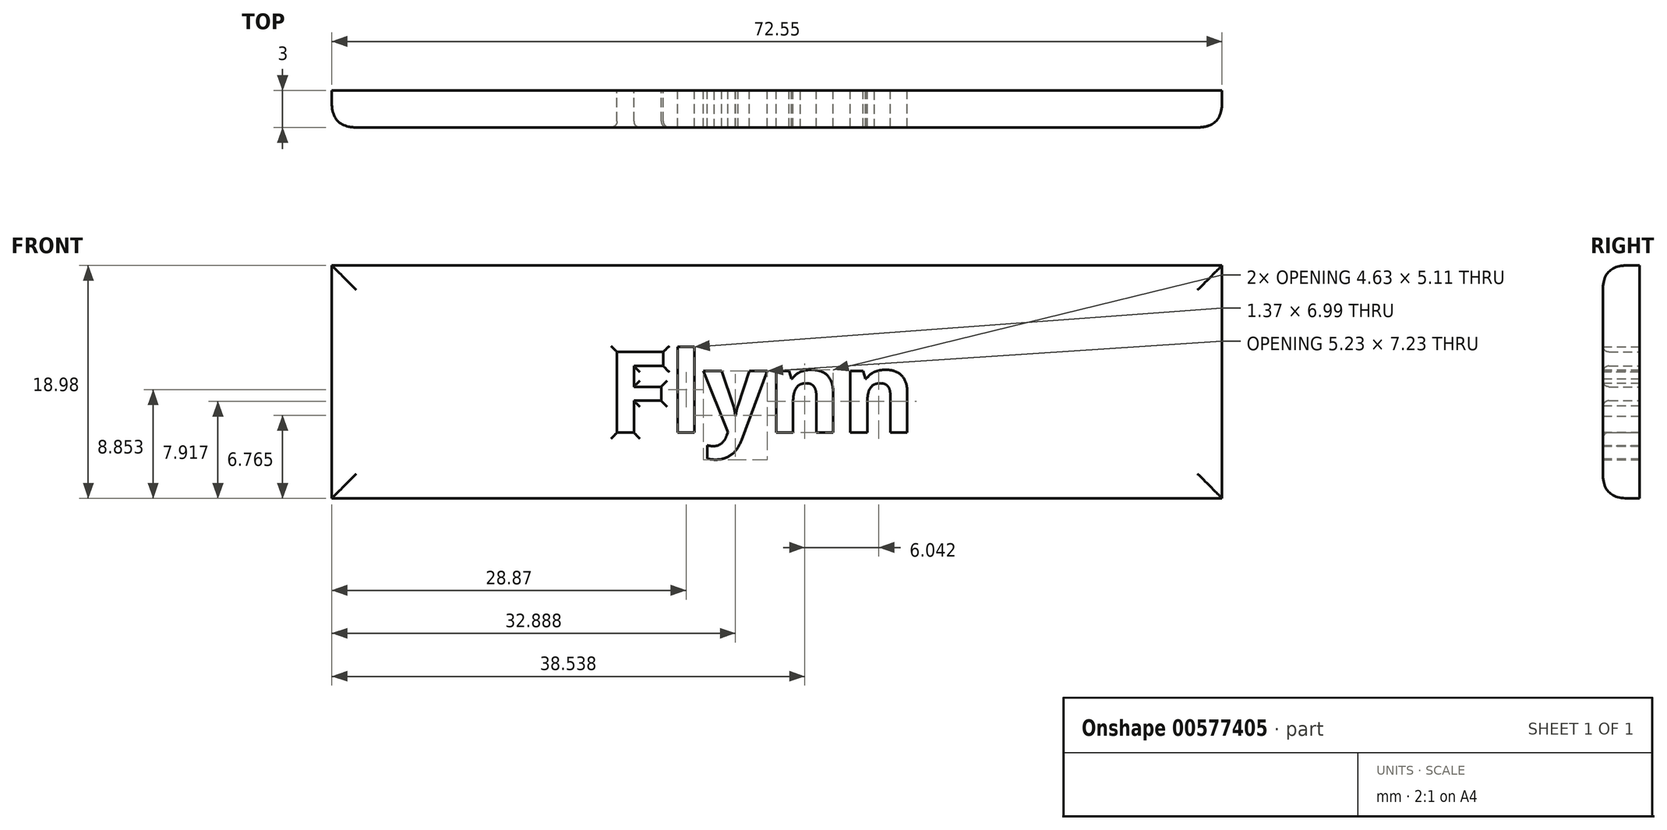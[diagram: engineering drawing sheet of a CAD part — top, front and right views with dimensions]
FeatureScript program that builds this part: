
annotation { "Feature Type Name" : "Feature", "Feature Type Description" : "" }
export const myFeature = defineFeature(function(context is Context, id is Id, definition is map)
    precondition{}
    {
        {
            var Q0;
            Q0=qCreatedBy(makeId("Front.planeOp"),FACE);
            var sketch = newSketch(context, id + "F0", { "sketchPlane" : qUnion([Q0])});
            skLineSegment(sketch, "E0.bottom", {"start": v(0, 0) * mm, "end": v(-72.55, 0) * mm});
            skLineSegment(sketch, "E0.top", {"start": v(0, 18.98) * mm, "end": v(-72.55, 18.98) * mm});
            skLineSegment(sketch, "E0.left", {"start": v(0, 0) * mm, "end": v(0, 18.98) * mm});
            skLineSegment(sketch, "E0.right", {"start": v(-72.55, 0) * mm, "end": v(-72.55, 18.98) * mm});
            skText(sketch, "E1", { "text": "Flynn", "fontName": "OpenSans-Bold.ttf"});
            const initialGuessF0  = {"E1": [-0.05013, 0.00536, 1, 0, 0.00662]};
            skSetInitialGuess(sketch, initialGuessF0);
            skSolve(sketch);
        }
        {
            var Q0;
            Q0=makeQuery(id+"F0.imprint","IMPRINT",FACE,{"disambiguationData":[TD([[makeQuery(id+"F0.imprint","IMPRINT",EDGE,{"derivedFrom":sQuery(id+"F0.wireOp",EDGE,"E0.bottom")}),-1.0]])]});
            extrude(context, id + "F1", {"entities" : qUnion([Q0]), "depth" : 3 * mm, "offsetDistance" : 25 * mm});
        }
        {
            var Q0;
            Q0=makeQuery(id+"F1.opExtrude","CAP_EDGE",EDGE,{"disambiguationData":[OSD([sQuery(id+"F0.wireOp",EDGE,"E0.top")])],"isStart":false});
            var Q1;
            Q1=makeQuery(id+"F1.opExtrude","CAP_EDGE",EDGE,{"disambiguationData":[OSD([sQuery(id+"F0.wireOp",EDGE,"E0.right")])],"isStart":false});
            var Q2;
            Q2=makeQuery(id+"F1.opExtrude","CAP_EDGE",EDGE,{"disambiguationData":[OSD([sQuery(id+"F0.wireOp",EDGE,"E0.bottom")])],"isStart":false});
            var Q3;
            Q3=makeQuery(id+"F1.opExtrude","CAP_EDGE",EDGE,{"disambiguationData":[OSD([sQuery(id+"F0.wireOp",EDGE,"E0.left")])],"isStart":false});
            fillet(context, id + "F2", {"entities" : qUnion([Q0, Q1, Q2, Q3]), "radius" : 2 * mm, "rho" : 0.5, "crossSection" : FilletCrossSection.CONIC, "allowEdgeOverflow" : false});
        }
        {
            var Q0;
            Q0=makeQuery(id+"F1.opExtrude","CAP_EDGE",EDGE,{"disambiguationData":[OSD([sQuery(id+"F0.wireOp",EDGE,"E1.sketch_text.stroke-1")])],"isStart":false});
            var Q1;
            Q1=makeQuery(id+"F1.opExtrude","CAP_EDGE",EDGE,{"disambiguationData":[OSD([sQuery(id+"F0.wireOp",EDGE,"E1.sketch_text.stroke-2")])],"isStart":false});
            var Q2;
            Q2=makeQuery(id+"F1.opExtrude","CAP_EDGE",EDGE,{"disambiguationData":[OSD([sQuery(id+"F0.wireOp",EDGE,"E1.sketch_text.stroke-3")])],"isStart":false});
            var Q3;
            Q3=makeQuery(id+"F1.opExtrude","CAP_EDGE",EDGE,{"disambiguationData":[OSD([sQuery(id+"F0.wireOp",EDGE,"E1.sketch_text.stroke-4")])],"isStart":false});
            var Q4;
            Q4=makeQuery(id+"F1.opExtrude","CAP_EDGE",EDGE,{"disambiguationData":[OSD([sQuery(id+"F0.wireOp",EDGE,"E1.sketch_text.stroke-5")])],"isStart":false});
            var Q5;
            Q5=makeQuery(id+"F1.opExtrude","CAP_EDGE",EDGE,{"disambiguationData":[OSD([sQuery(id+"F0.wireOp",EDGE,"E1.sketch_text.stroke-6")])],"isStart":false});
            var Q6;
            Q6=makeQuery(id+"F1.opExtrude","CAP_EDGE",EDGE,{"disambiguationData":[OSD([sQuery(id+"F0.wireOp",EDGE,"E1.sketch_text.stroke-7")])],"isStart":false});
            var Q7;
            Q7=makeQuery(id+"F1.opExtrude","CAP_EDGE",EDGE,{"disambiguationData":[OSD([sQuery(id+"F0.wireOp",EDGE,"E1.sketch_text.stroke-8")])],"isStart":false});
            var Q8;
            Q8=makeQuery(id+"F1.opExtrude","CAP_EDGE",EDGE,{"disambiguationData":[OSD([sQuery(id+"F0.wireOp",EDGE,"E1.sketch_text.stroke-9")])],"isStart":false});
            var Q9;
            Q9=makeQuery(id+"F1.opExtrude","CAP_EDGE",EDGE,{"disambiguationData":[OSD([sQuery(id+"F0.wireOp",EDGE,"E1.sketch_text.stroke-0")])],"isStart":false});
            fillet(context, id + "F3", {"entities" : qUnion([Q0, Q1, Q2, Q3, Q4, Q5, Q6, Q7, Q8, Q9]), "radius" : .5 * mm, "tangentPropagation" : true, "allowEdgeOverflow" : false});
        }
    });
